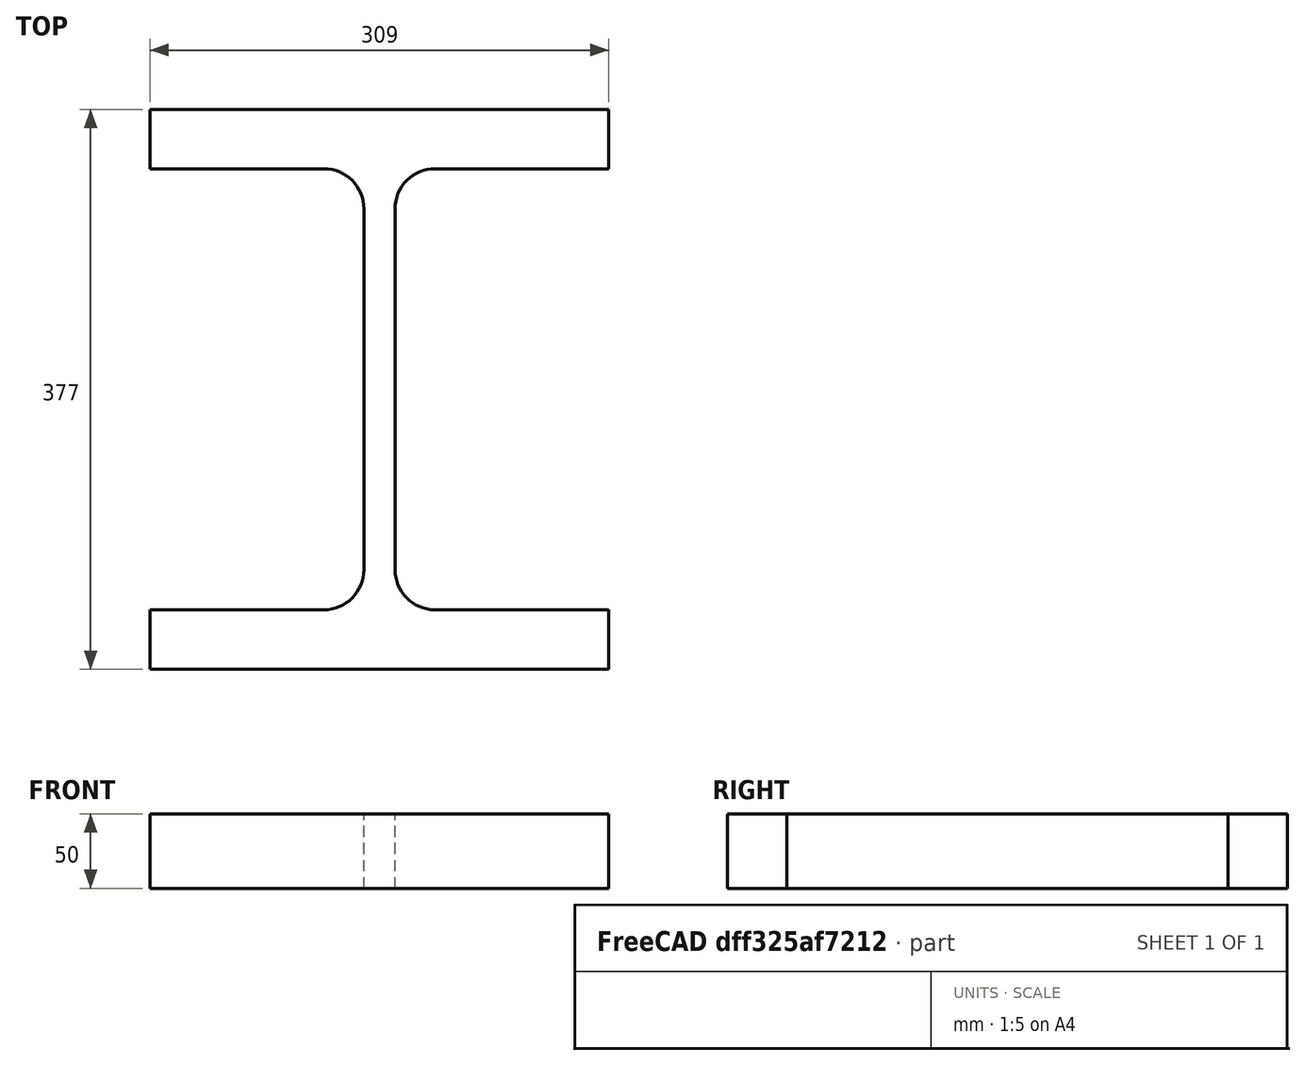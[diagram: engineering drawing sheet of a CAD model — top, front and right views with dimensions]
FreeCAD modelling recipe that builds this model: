
FCSTD DOCUMENT  (FreeCAD 0.15R4671 (Git))
Label: HE-M-Profile 340 DIN1025-4 S235JR
License: All rights reserved
LicenseURL: http://en.wikipedia.org/wiki/All_rights_reserved
objects: Sketcher::SketchObject×1, Part::Extrusion×1
note: 2 computed .brp shape members not serialized (recipe doc carries the construction recipe); baked Part::Feature solids carry a one-line shape summary decoded from their .brp

FEATURE [Sketcher::SketchObject] Sketch
  sketch-geometry (16):
    g0: LineSegment StartX=10.5 StartY=-121.5 StartZ=0 EndX=10.5 EndY=121.5 EndZ=0
    g1: LineSegment StartX=37.5 StartY=148.5 StartZ=0 EndX=154.5 EndY=148.5 EndZ=0
    g2: LineSegment StartX=154.5 StartY=148.5 StartZ=0 EndX=154.5 EndY=188.5 EndZ=0
    g3: LineSegment StartX=154.5 StartY=188.5 StartZ=0 EndX=-154.5 EndY=188.5 EndZ=0
    g4: LineSegment StartX=-154.5 StartY=188.5 StartZ=0 EndX=-154.5 EndY=148.5 EndZ=0
    g5: LineSegment StartX=-154.5 StartY=148.5 StartZ=0 EndX=-37.5 EndY=148.5 EndZ=0
    g6: LineSegment StartX=-10.5 StartY=121.5 StartZ=0 EndX=-10.5 EndY=-121.5 EndZ=0
    g7: LineSegment StartX=-37.5 StartY=-148.5 StartZ=0 EndX=-154.5 EndY=-148.5 EndZ=0
    g8: LineSegment StartX=-154.5 StartY=-148.5 StartZ=0 EndX=-154.5 EndY=-188.5 EndZ=0
    g9: LineSegment StartX=-154.5 StartY=-188.5 StartZ=0 EndX=154.5 EndY=-188.5 EndZ=0
    g10: LineSegment StartX=154.5 StartY=-188.5 StartZ=0 EndX=154.5 EndY=-148.5 EndZ=0
    g11: LineSegment StartX=154.5 StartY=-148.5 StartZ=0 EndX=37.5 EndY=-148.5 EndZ=0
    g12: ArcOfCircle CenterX=37.5 CenterY=121.5 CenterZ=0 NormalX=0 NormalY=0 NormalZ=1 Radius=27 StartAngle=1.5708 EndAngle=3.14159
    g13: ArcOfCircle CenterX=37.5 CenterY=-121.5 CenterZ=0 NormalX=0 NormalY=0 NormalZ=1 Radius=27 StartAngle=3.14159 EndAngle=4.71239
    g14: ArcOfCircle CenterX=-37.5 CenterY=121.5 CenterZ=0 NormalX=0 NormalY=0 NormalZ=1 Radius=27 StartAngle=0 EndAngle=1.5708
    g15: ArcOfCircle CenterX=-37.5 CenterY=-121.5 CenterZ=0 NormalX=0 NormalY=0 NormalZ=1 Radius=27 StartAngle=4.71239 EndAngle=6.28319
  constraints (42):
    c: Vertical(g0)
    c: Coincident(g2,g1)
    c: Vertical(g2)
    c: Coincident(g3,g2)
    c: Coincident(g4,g3)
    c: Vertical(g4)
    c: Coincident(g5,g4)
    c: Horizontal(g5)
    c: Vertical(g6)
    c: Horizontal(g7)
    c: Coincident(g8,g7)
    c: Vertical(g8)
    c: Coincident(g9,g8)
    c: Horizontal(g9)
    c: Coincident(g10,g9)
    c: Vertical(g10)
    c: Coincident(g11,g10)
    c: Horizontal(g11)
    c: Tangent(g1,g12) = 1.5708
    c: Tangent(g0,g12) = 1.5708
    c: Tangent(g0,g13) = 1.5708
    c: Tangent(g11,g13) = 1.5708
    c: Tangent(g5,g14) = 1.5708
    c: Tangent(g6,g14) = 1.5708
    c: Tangent(g6,g15) = 1.5708
    c: Tangent(g7,g15) = 1.5708
    c: Equal(g3,g9)
    c: Equal(g2,g4)
    c: Equal(g4,g8)
    c: Equal(g8,g10)
    c: Equal(g12,g14)
    c: Equal(g14,g15)
    c: Equal(g15,g13)
    c: Symmetric(g2,g3,g-2)
    c: Symmetric(g9,g8,g-2)
    c: Symmetric(g0,g6,g-2)
    c: Symmetric(g2,g9,g-1)
    c: DistanceY(g2,g9) = -377
    c: DistanceX(g3) = -309
    c: DistanceX(g0,g6) = -21
    c: DistanceY(g2) = 40
    c: Radius(g12) = 27
FEATURE [Part::Extrusion] Extrude  label="HE-M-Profile 340 DIN1025-4 S235JR"
  Base = -> Sketch
  Dir = (0,0,50)
  Solid = true
